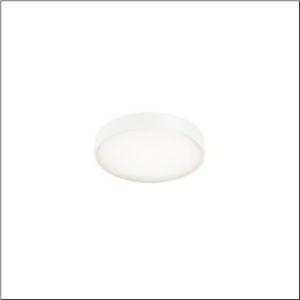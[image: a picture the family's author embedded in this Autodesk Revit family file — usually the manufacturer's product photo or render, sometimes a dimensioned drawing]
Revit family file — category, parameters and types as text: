
# Revit family: round_21_s_51mr34fd0421w
name_source: partatom
category: Lighting Fixtures
units: mm (PartAtom-declared; Revit-internal decimal feet)

## family parameters
Cut with Voids When Loaded = No
Host = Face
Light Source = No
Part Type = Normal
Room Calculation Point = No
Round Connector Dimension = Use Diameter
Shared = No

## types (1)
- Round 21 S (1 x LED, 3910 lm, 30.3 W, 4000K)
    Apparent Load = 30 VA
    CIE Flux Codes = 49 80 96 100 100
    Color Rendering = 80
    Color Temperature = 4000K
    Default Elevation = 1800 mm
    Description = Round 21 S, wall and ceiling luminaire, primary optical cover: cover, of PMMA, opal, light emission: direct distribution, primary light characteristic: symmetric, installation type: suspended mounting, surface-mounted, LED, rated luminous flux: 3.900lm, luminous efficacy: 129lm/W, light colour: 840, colour temperature: 4000K, control gear: DALI 2, with terminal, 5-pole, mains connection: 230V, AC, 50/60Hz, rated input power: 30.3W, housing, of aluminium, coated, white, diameter: 400mm, height: 62mm, protection rating (complete): IP40, insulation class (complete): insulation class I (protective earthing), certification: CE, impact resistance: IK04, permissible operating ambient temperature: -10..+35°C, packaging unit: 1 piece
    Height = 87 mm
    Lamp = 1 x LED
    Lamp Light Flux = 3910 lm
    Lamp Power = 30.3 W
    Lamp count = 1
    Length = 400 mm
    Luminous efficacy = 129 lm/W
    Manufacturer = Siteco
    ModVariant = No
    Model = 51MR34FD0421W
    Mounting Place = Ceiling
    Mounting Type = Surface mounted
    Number of Poles = 1
    OnlyDefault = Yes
    Power Factor = 1
    Product Name = Round 21 S
    Product group = wall and ceiling luminaire
    ProductGroupID = 304
    Protection Class = Protection class I
    Protection Degree = IP 40
    RLX_Detail_Level = 1
    RLX_Emergency_Light_Flux = 0 lm
    RLX_Emergency_Type = 0
    RLX_Emergency_Type_DB = No
    RlxData = <blob elided: 9513 chars, md5=d650cd0a>
    Socket = socket
    Standby Power = 0 W
    System Light Flux = 3910 lm
    System Power = 30 W
    Type Comments = Product without accessories
    Type Image = l_1258307.jpg
    URL = http://relux.com
    VarID = ---
    Voltage = 0 V
    Weight = 0.00 kg
    Width = 0 mm  [stored 0 ft]

note: [stored X ft] marks values corroborated as IEEE doubles in the binary element streams (Revit-internal decimal feet)

## geometry (parser evidence)
native form markers: Sweep x9
no freeform markers — native parametric forms only
